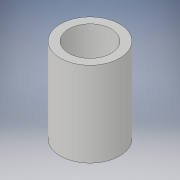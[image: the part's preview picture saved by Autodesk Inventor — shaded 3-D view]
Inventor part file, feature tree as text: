
AUTODESK INVENTOR PART (.ipt)
format: ipt  version: 2019.4 (Build 234330000, 330)  size: 94,720 bytes
history: native  units: mm
features: extrude x1, sketch x1
ambient origin geometry x8: Origin, YZ Plane, XZ Plane, XY Plane, X Axis, Y Axis, Z Axis, Center Point
bodies: Solid1 (feature_tree)
feature tree (2):
  extrude  "Extrusion1"  Depth=10.0mm
  sketch  "Sketch1"  dims[d0=5.0mm d1=7.0mm d2=10.0mm d3=0.0mm]
